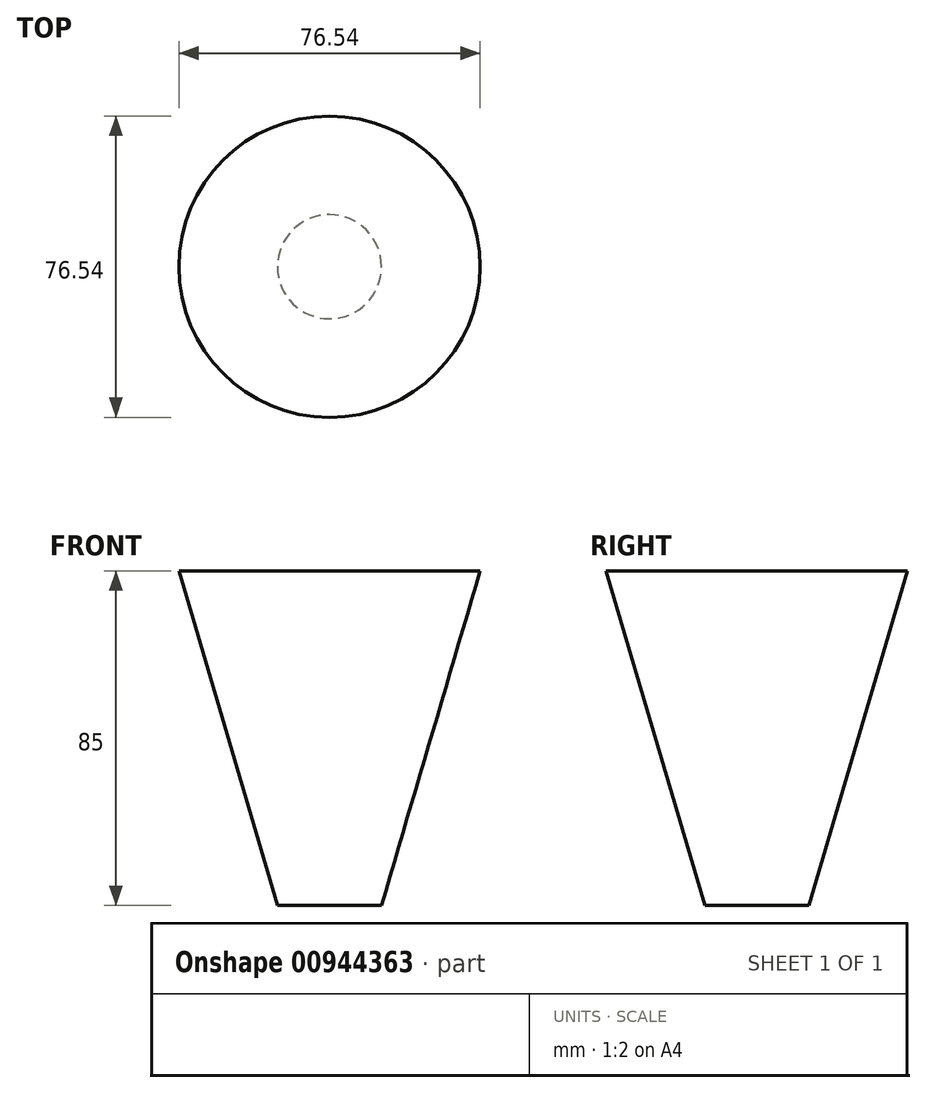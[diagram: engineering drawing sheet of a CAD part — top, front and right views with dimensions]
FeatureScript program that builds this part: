
annotation { "Feature Type Name" : "Feature", "Feature Type Description" : "" }
export const myFeature = defineFeature(function(context is Context, id is Id, definition is map)
    precondition{}
    {
        {
            var Q0;
            Q0=qCreatedBy(makeId("Top.planeOp"),FACE);
            cPlane(context, id + "F0", {"entities" : qUnion([Q0]), "cplaneType" : CPlaneType.OFFSET, "offset" : 85 * mm, "width" : 150 * mm, "height" : 150 * mm});
        }
        {
            var Q0;
            Q0=qCreatedBy(id+"F0.planeOp",FACE);
            var sketch = newSketch(context, id + "F1", { "sketchPlane" : qUnion([Q0])});
            skCircle(sketch, "E0", {"center": v(0, 0) * mm, "radius": 38.27 * mm});
            skSolve(sketch);
        }
        {
            var Q0;
            Q0=qCreatedBy(makeId("Top.planeOp"),FACE);
            cPlane(context, id + "F2", {"entities" : qUnion([Q0]), "cplaneType" : CPlaneType.OFFSET, "offset" : 25 * mm, "width" : 150 * mm, "height" : 150 * mm});
        }
        {
            var Q0;
            Q0=qCreatedBy(makeId("Top.planeOp"),FACE);
            var sketch = newSketch(context, id + "F3", { "sketchPlane" : qUnion([Q0])});
            skCircle(sketch, "E1", {"center": v(0, 0) * mm, "radius": 13.22 * mm});
            skSolve(sketch);
        }
        {
            var Q0;
            Q0=makeQuery(id+"F3.imprint","IMPRINT",FACE,{"disambiguationData":[TD([[makeQuery(id+"F3.imprint","IMPRINT",EDGE,{"derivedFrom":sQuery(id+"F3.wireOp",EDGE,"E1")}),1.0]])]});
            var Q1;
            Q1=makeQuery(id+"F1.imprint","IMPRINT",FACE,{"disambiguationData":[TD([[makeQuery(id+"F1.imprint","IMPRINT",EDGE,{"derivedFrom":sQuery(id+"F1.wireOp",EDGE,"E0")}),1.0]])]});
            loft(context, id + "F4", {"sheetProfilesArray" : [{ "sheetProfileEntities" : qUnion([Q0]) }, { "sheetProfileEntities" : qUnion([Q1]) }]});
        }
    });
